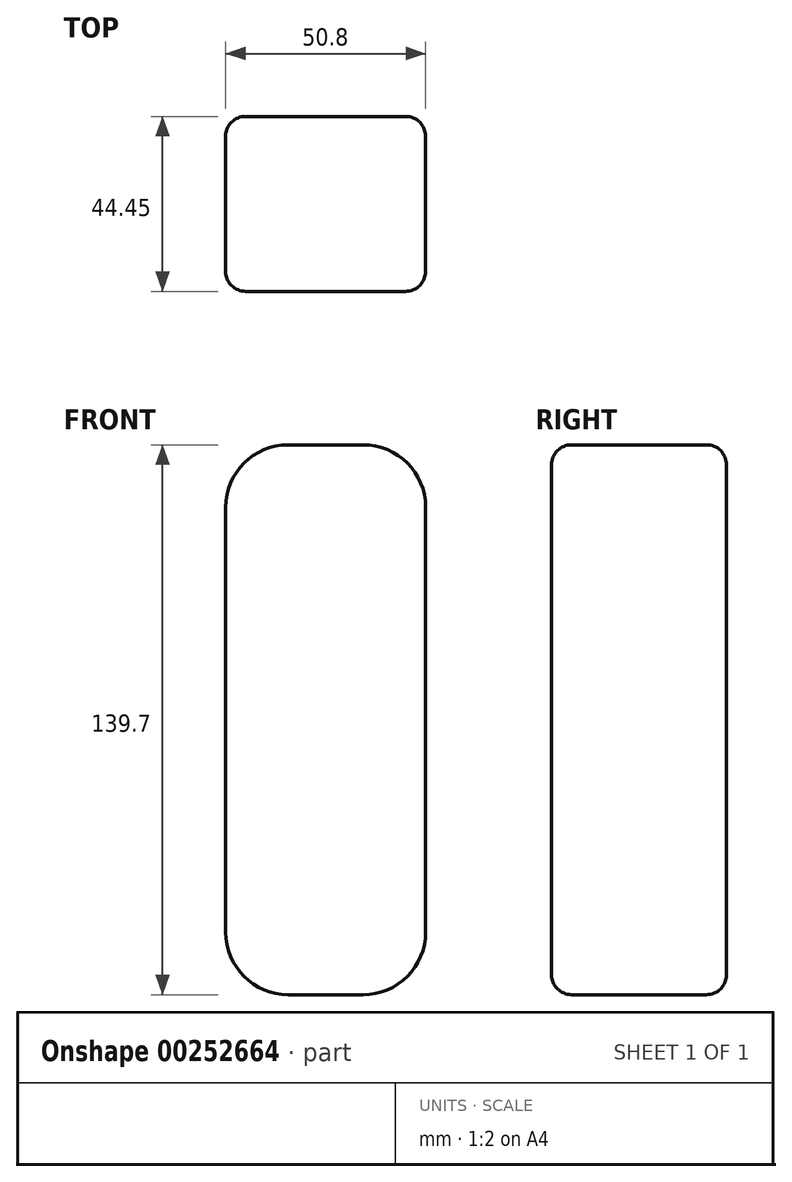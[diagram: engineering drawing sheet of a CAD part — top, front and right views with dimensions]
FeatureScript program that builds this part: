
annotation { "Feature Type Name" : "Feature", "Feature Type Description" : "" }
export const myFeature = defineFeature(function(context is Context, id is Id, definition is map)
    precondition{}
    {
        {
            var Q0;
            Q0=qCreatedBy(makeId("Front.planeOp"),FACE);
            var sketch = newSketch(context, id + "F0", { "sketchPlane" : qUnion([Q0])});
            skLineSegment(sketch, "E0.bottom", {"start": v(9.52, 69.85) * mm, "end": v(-9.53, 69.85) * mm});
            skLineSegment(sketch, "E0.top", {"start": v(9.53, -69.85) * mm, "end": v(-9.52, -69.85) * mm});
            skLineSegment(sketch, "E0.left", {"start": v(25.4, 53.98) * mm, "end": v(25.4, -53.98) * mm});
            skLineSegment(sketch, "E0.right", {"start": v(-25.4, 53.98) * mm, "end": v(-25.4, -53.98) * mm});
            skPoint(sketch, "E0.middle", {"position": v(0, 0) * mm});
            skPoint(sketch, "E1.visualSharp", {"position": v(-25.4, 69.85) * mm});
            skArc(sketch, "E1.filletArc", {"start": v(-9.53, 69.85) * mm, "mid": v(-20.75, 65.2) * mm, "end": v(-25.4, 53.98) * mm});
            skPoint(sketch, "E2.visualSharp", {"position": v(25.4, 69.85) * mm});
            skArc(sketch, "E2.filletArc", {"start": v(25.4, 53.98) * mm, "mid": v(20.75, 65.2) * mm, "end": v(9.52, 69.85) * mm});
            skPoint(sketch, "E3.visualSharp", {"position": v(25.4, -69.85) * mm});
            skArc(sketch, "E3.filletArc", {"start": v(9.53, -69.85) * mm, "mid": v(20.75, -65.2) * mm, "end": v(25.4, -53.98) * mm});
            skPoint(sketch, "E4.visualSharp", {"position": v(-25.4, -69.85) * mm});
            skArc(sketch, "E4.filletArc", {"start": v(-25.4, -53.98) * mm, "mid": v(-20.75, -65.2) * mm, "end": v(-9.52, -69.85) * mm});
            skSolve(sketch);
        }
        {
            var Q0;
            Q0=makeQuery(id+"F0.imprint","IMPRINT",FACE,{"disambiguationData":[TD([[makeQuery(id+"F0.imprint","IMPRINT",EDGE,{"derivedFrom":sQuery(id+"F0.wireOp",EDGE,"E0.bottom")}),1.0]])]});
            extrude(context, id + "F1", {"entities" : qUnion([Q0]), "depth" : 44.45 * mm});
        }
        {
            var Q0;
            Q0=makeQuery(id+"F1.opExtrude","SWEPT_FACE",FACE,{"disambiguationData":[OSD([sQuery(id+"F0.wireOp",EDGE,"E1.filletArc")])]});
            var Q1;
            Q1=makeQuery(id+"F1.opExtrude","CAP_FACE",FACE,{"disambiguationData":[OSD([sQuery(id+"F0.wireOp",EDGE,"E0.bottom"),sQuery(id+"F0.wireOp",EDGE,"E0.top"),sQuery(id+"F0.wireOp",EDGE,"E0.left"),sQuery(id+"F0.wireOp",EDGE,"E0.right"),sQuery(id+"F0.wireOp",EDGE,"E1.filletArc"),sQuery(id+"F0.wireOp",EDGE,"E2.filletArc"),sQuery(id+"F0.wireOp",EDGE,"E3.filletArc"),sQuery(id+"F0.wireOp",EDGE,"E4.filletArc")])],"isStart":true});
            fillet(context, id + "F2", {"entities" : qUnion([Q0, Q1]), "radius" : 5.08 * mm, "tangentPropagation" : true, "allowEdgeOverflow" : false});
        }
    });
